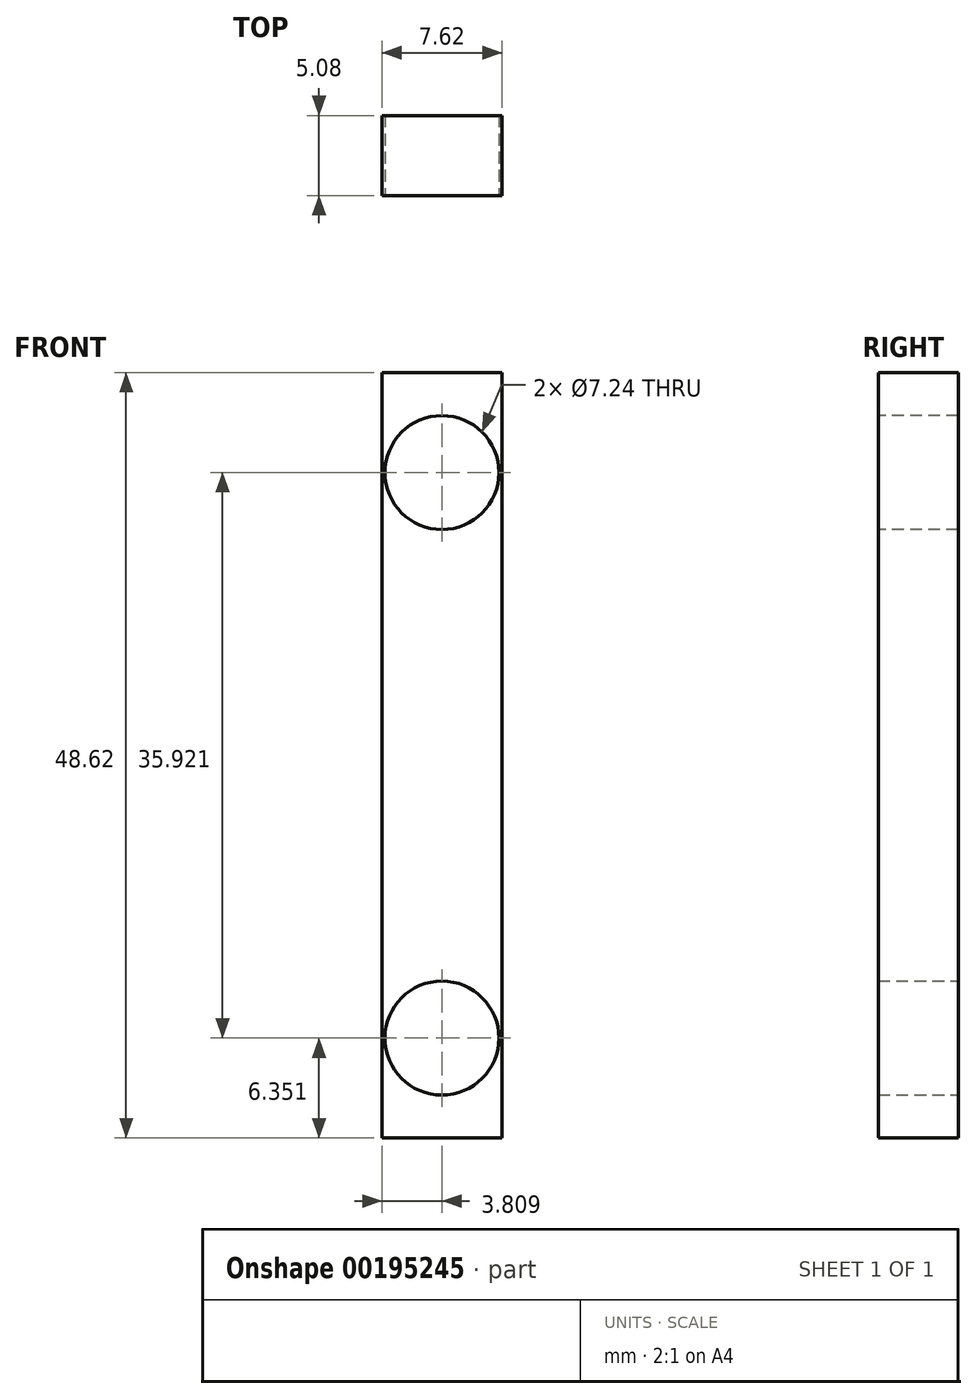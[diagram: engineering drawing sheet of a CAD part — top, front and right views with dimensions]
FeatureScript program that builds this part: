
annotation { "Feature Type Name" : "Feature", "Feature Type Description" : "" }
export const myFeature = defineFeature(function(context is Context, id is Id, definition is map)
    precondition{}
    {
        {
            var Q0;
            Q0=qCreatedBy(makeId("Front.planeOp"),FACE);
            var sketch = newSketch(context, id + "F0", { "sketchPlane" : qUnion([Q0])});
            skLineSegment(sketch, "E0.bottom", {"start": v(-7.57, 39.84) * mm, "end": v(0.05, 39.84) * mm});
            skLineSegment(sketch, "E0.top", {"start": v(-7.57, -8.78) * mm, "end": v(0.05, -8.78) * mm});
            skLineSegment(sketch, "E0.left", {"start": v(-7.57, 39.84) * mm, "end": v(-7.57, -8.78) * mm});
            skLineSegment(sketch, "E0.right", {"start": v(0.05, 39.84) * mm, "end": v(0.05, -8.78) * mm});
            skSolve(sketch);
        }
        {
            var Q0;
            Q0 = qSketchRegion(id + "F0", true);
            extrude(context, id + "F1", {"entities" : qUnion([Q0]), "depth" : 5.08 * mm});
        }
        {
            var Q0;
            Q0=makeQuery(id+"F1.opExtrude","CAP_FACE",FACE,{"disambiguationData":[OSD([sQuery(id+"F0.wireOp",EDGE,"E0.bottom"),sQuery(id+"F0.wireOp",EDGE,"E0.top"),sQuery(id+"F0.wireOp",EDGE,"E0.left"),sQuery(id+"F0.wireOp",EDGE,"E0.right")])],"isStart":false});
            var sketch = newSketch(context, id + "F2", { "sketchPlane" : qUnion([Q0])});
            skCircle(sketch, "E1", {"center": v(-3.76, 33.5) * mm, "radius": 3.62 * mm, "construction": true});
            skPoint(sketch, "E1.centerSnap0", {"position": v(-3.76, 39.84) * mm});
            skSolve(sketch);
        }
        {
            var Q0;
            Q0=qCreatedBy(makeId("Front.planeOp"),FACE);
            var sketch = newSketch(context, id + "F3", { "sketchPlane" : qUnion([Q0])});
            skCircle(sketch, "E2", {"center": v(-3.76, -2.43) * mm, "radius": 3.62 * mm, "construction": true});
            skSolve(sketch);
        }
        {
            var Q0;
            Q0=sQuery(id+"F2.wireOp",VERTEX,"E1.center");
            var Q1;
            Q1=makeQuery(id+"F1.opExtrude","SWEPT_BODY",BODY,{"disambiguationData":[OSD([sQuery(id+"F0.wireOp",EDGE,"E0.bottom"),sQuery(id+"F0.wireOp",EDGE,"E0.top"),sQuery(id+"F0.wireOp",EDGE,"E0.left"),sQuery(id+"F0.wireOp",EDGE,"E0.right")])]});
            hole(context, id + "F4", {"style" : HoleStyle.SIMPLE, "endStyle" : HoleEndStyle.THROUGH, "holeDiameter" : 7.24 * mm, "locations" : qUnion([Q0]), "scope" : qUnion([Q1]), "isTappedThrough" : true});
        }
        {
            var Q0;
            Q0=sQuery(id+"F3.wireOp",VERTEX,"E2.center");
            var Q1;
            Q1=makeQuery(id+"F1.opExtrude","SWEPT_BODY",BODY,{"disambiguationData":[OSD([sQuery(id+"F0.wireOp",EDGE,"E0.bottom"),sQuery(id+"F0.wireOp",EDGE,"E0.top"),sQuery(id+"F0.wireOp",EDGE,"E0.left"),sQuery(id+"F0.wireOp",EDGE,"E0.right")])]});
            hole(context, id + "F5", {"style" : HoleStyle.SIMPLE, "endStyle" : HoleEndStyle.THROUGH, "oppositeDirection" : true, "holeDiameter" : 7.24 * mm, "locations" : qUnion([Q0]), "scope" : qUnion([Q1]), "isTappedThrough" : true});
        }
    });
